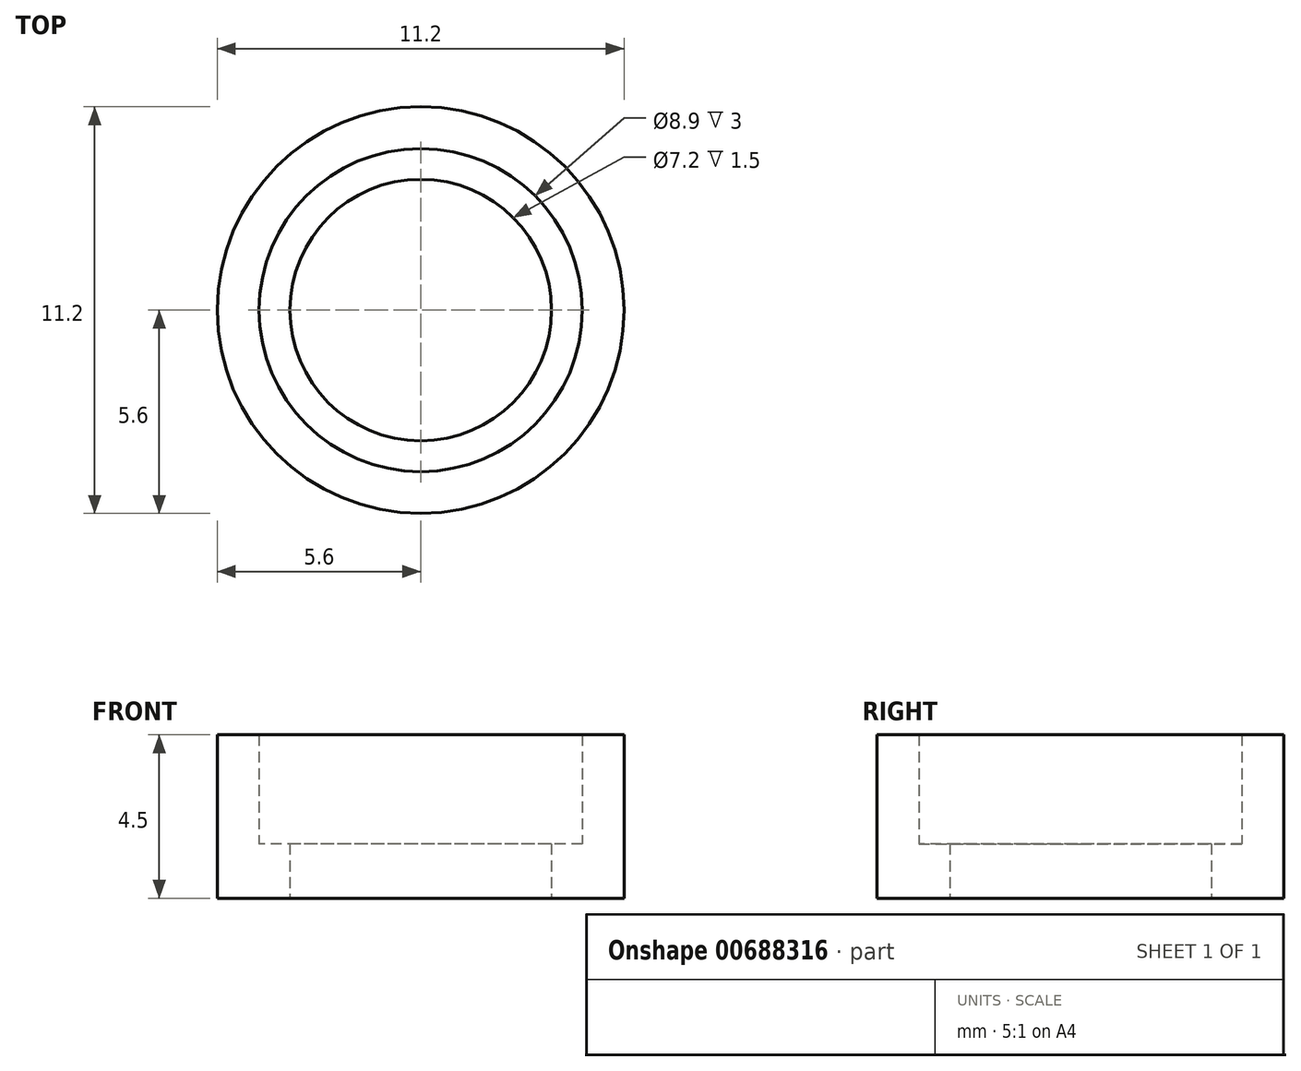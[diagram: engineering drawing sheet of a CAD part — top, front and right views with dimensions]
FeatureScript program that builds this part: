
annotation { "Feature Type Name" : "Feature", "Feature Type Description" : "" }
export const myFeature = defineFeature(function(context is Context, id is Id, definition is map)
    precondition{}
    {
        {
            var Q0;
            Q0=qCreatedBy(makeId("Top.planeOp"),FACE);
            var sketch = newSketch(context, id + "F0", { "sketchPlane" : qUnion([Q0])});
            skCircle(sketch, "E0", {"center": v(0, 0) * mm, "radius": 4.45 * mm});
            skCircle(sketch, "E1", {"center": v(0, 0) * mm, "radius": 5.6 * mm});
            skSolve(sketch);
        }
        {
            var Q0;
            Q0=makeQuery(id+"F0.imprint","IMPRINT",FACE,{"disambiguationData":[TD([[makeQuery(id+"F0.imprint","IMPRINT",EDGE,{"derivedFrom":sQuery(id+"F0.wireOp",EDGE,"E0")}),-1.0]])]});
            extrude(context, id + "F1", {"entities" : qUnion([Q0]), "depth" : 4.5 * mm, "offsetDistance" : 25 * mm});
        }
        {
            var Q0;
            Q0=qCreatedBy(makeId("Top.planeOp"),FACE);
            var sketch = newSketch(context, id + "F2", { "sketchPlane" : qUnion([Q0])});
            skCircle(sketch, "E2", {"center": v(0, 0) * mm, "radius": 3.6 * mm});
            skCircle(sketch, "E3.0", {"center": v(0, 0) * mm, "radius": 4.45 * mm});
            skSolve(sketch);
        }
        {
            var Q0;
            Q0=makeQuery(id+"F2.imprint","IMPRINT",FACE,{"disambiguationData":[TD([[makeQuery(id+"F2.imprint","IMPRINT",EDGE,{"derivedFrom":sQuery(id+"F2.wireOp",EDGE,"E2")}),-1.0]])]});
            extrude(context, id + "F3", {"entities" : qUnion([Q0]), "operationType" : NewBodyOperationType.ADD, "depth" : 1.5 * mm, "offsetDistance" : 25 * mm});
        }
    });
